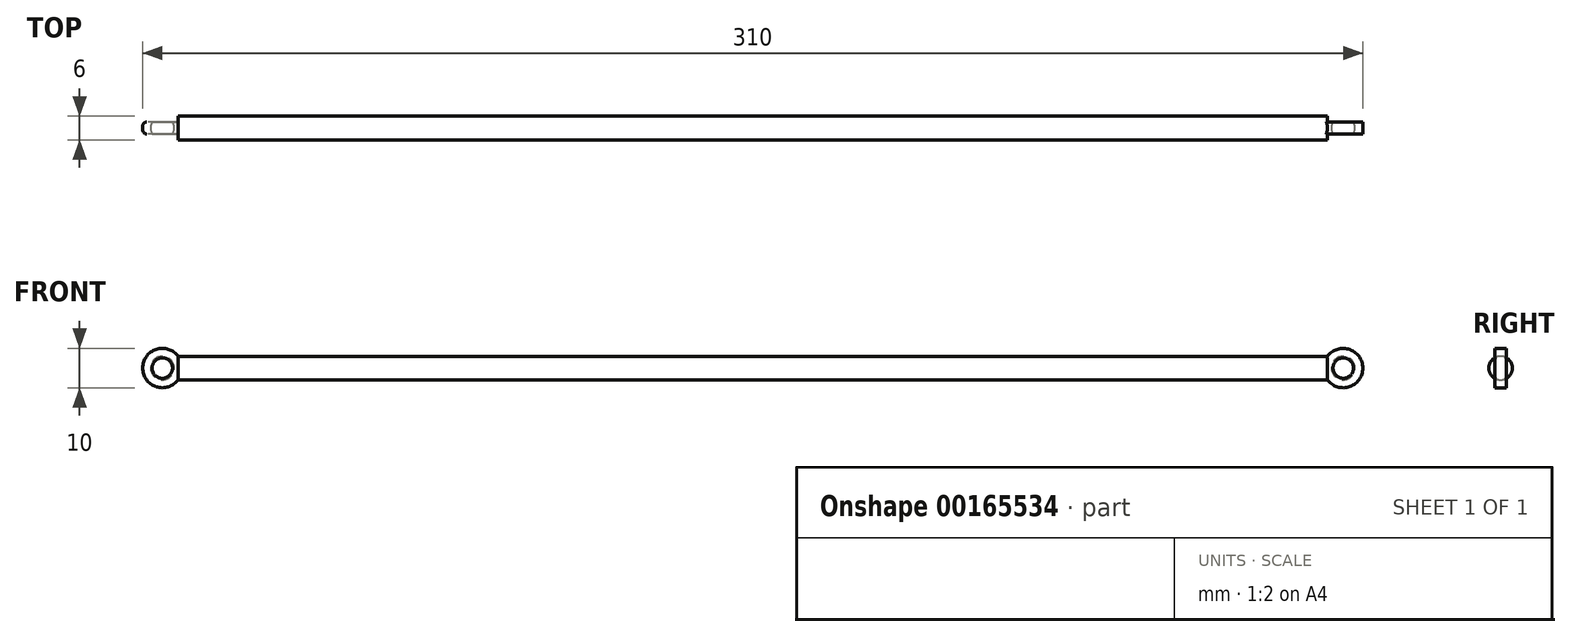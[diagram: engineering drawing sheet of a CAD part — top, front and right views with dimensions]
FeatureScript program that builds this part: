
annotation { "Feature Type Name" : "Feature", "Feature Type Description" : "" }
export const myFeature = defineFeature(function(context is Context, id is Id, definition is map)
    precondition{}
    {
        {
            var Q0;
            Q0=qCreatedBy(makeId("Top.planeOp"),FACE);
            var sketch = newSketch(context, id + "F0", { "sketchPlane" : qUnion([Q0])});
            skArc(sketch, "E0", {"start": v(1.5, -2.6) * mm, "mid": v(3, 0) * mm, "end": v(1.5, 2.6) * mm});
            skLineSegment(sketch, "E1", {"start": v(0, 16.17) * mm, "end": v(0, -15.14) * mm, "construction": true});
            skLineSegment(sketch, "E2.right", {"start": v(1.5, 2.6) * mm, "end": v(1.5, -2.6) * mm});
            skSolve(sketch);
        }
        {
            var Q0;
            Q0=qCreatedBy(makeId("Front.planeOp"),FACE);
            var sketch = newSketch(context, id + "F1", { "sketchPlane" : qUnion([Q0])});
            skCircle(sketch, "E3", {"center": v(0, 0) * mm, "radius": 5 * mm});
            skCircle(sketch, "E4", {"center": v(0, 0) * mm, "radius": 2 * mm});
            skSolve(sketch);
        }
        {
            var Q0;
            Q0 = qSketchRegion(id + "F1", true);
            extrude(context, id + "F2", {"entities" : qUnion([Q0]), "endBound" : BoundingType.SYMMETRIC, "depth" : 3 * mm});
        }
        {
            var Q0;
            Q0=makeQuery(id+"F0.imprint","IMPRINT",FACE,{"disambiguationData":[TD([[makeQuery(id+"F0.imprint","IMPRINT",EDGE,{"derivedFrom":sQuery(id+"F0.wireOp",EDGE,"E0")}),1.0]])]});
            var Q1;
            Q1=sQuery(id+"F0.wireOp",EDGE,"E1");
            revolve(context, id + "F3", {"operationType" : NewBodyOperationType.REMOVE, "entities" : qUnion([Q0]), "axis" : qUnion([Q1]), "revolveType" : RevolveType.FULL});
        }
        {
            var Q0;
            Q0=qCreatedBy(makeId("Right.planeOp"),FACE);
            cPlane(context, id + "F4", {"entities" : qUnion([Q0]), "cplaneType" : CPlaneType.OFFSET, "offset" : 4 * mm, "width" : 150 * mm, "height" : 150 * mm});
        }
        {
            var Q0;
            Q0=qCreatedBy(id+"F4.planeOp",FACE);
            var sketch = newSketch(context, id + "F5", { "sketchPlane" : qUnion([Q0])});
            skCircle(sketch, "E5", {"center": v(0, 0) * mm, "radius": 3 * mm});
            skSolve(sketch);
        }
        {
            var Q0;
            Q0=makeQuery(id+"F5.imprint","IMPRINT",FACE,{"disambiguationData":[TD([[makeQuery(id+"F5.imprint","IMPRINT",EDGE,{"derivedFrom":sQuery(id+"F5.wireOp",EDGE,"E5")}),1.0]])]});
            extrude(context, id + "F6", {"entities" : qUnion([Q0]), "operationType" : NewBodyOperationType.ADD, "depth" : 146 * mm});
        }
        {
            var Q0;
            Q0=makeQuery(id+"F6.opExtrude","CAP_FACE",FACE,{"disambiguationData":[OSD([sQuery(id+"F5.wireOp",EDGE,"E5")])],"isStart":false});
            cPlane(context, id + "F7", {"entities" : qUnion([Q0]), "cplaneType" : CPlaneType.OFFSET, "offset" : 0 * mm, "width" : 150 * mm, "height" : 150 * mm});
        }
        {
            var Q0;
            Q0=makeQuery(id+"F2.opExtrude","SWEPT_BODY",BODY,{"disambiguationData":[OSD([sQuery(id+"F1.wireOp",EDGE,"E3"),sQuery(id+"F1.wireOp",EDGE,"E4")])]});
            var Q1;
            Q1=qCreatedBy(id+"F7.planeOp",FACE);
            mirror(context, id + "F8", {"operationType" : NewBodyOperationType.ADD, "entities" : qUnion([Q0]), "mirrorPlane" : qUnion([Q1])});
        }
        {
            var Q0;
            Q0=makeQuery(id+"F2.opExtrude","CAP_EDGE",EDGE,{"disambiguationData":[OSD([sQuery(id+"F1.wireOp",EDGE,"E3")])],"isStart":false});
            var Q1;
            Q1=makeQuery(id+"F2.opExtrude","CAP_EDGE",EDGE,{"disambiguationData":[OSD([sQuery(id+"F1.wireOp",EDGE,"E3")])],"isStart":true});
            fillet(context, id + "F9", {"entities" : qUnion([Q0, Q1]), "radius" : 1 * mm, "allowEdgeOverflow" : false});
        }
    });
